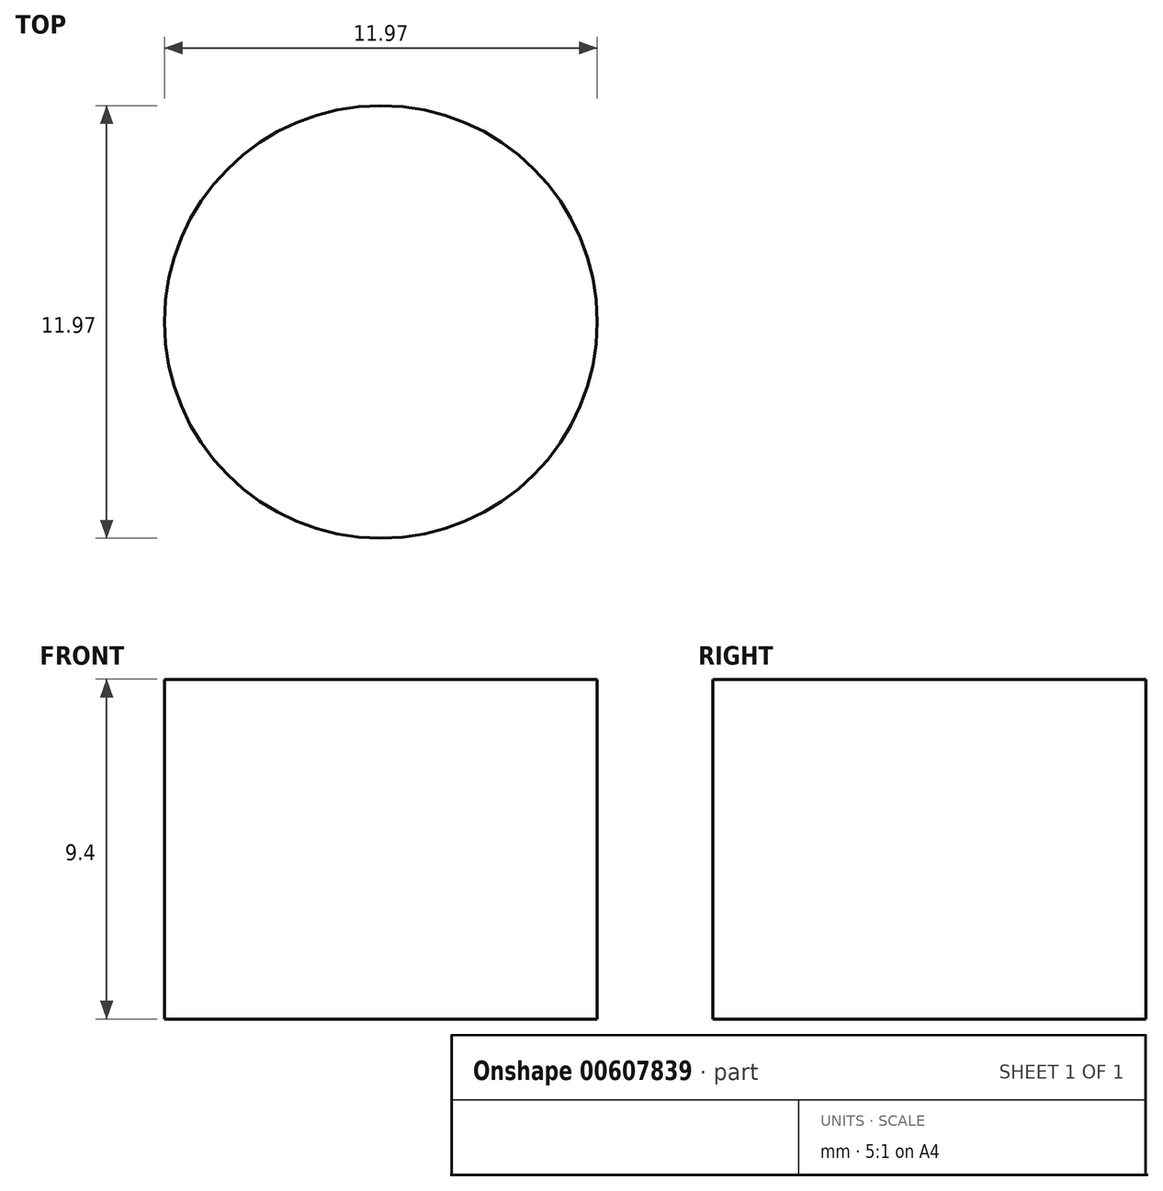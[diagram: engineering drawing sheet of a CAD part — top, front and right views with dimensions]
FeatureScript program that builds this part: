
annotation { "Feature Type Name" : "Feature", "Feature Type Description" : "" }
export const myFeature = defineFeature(function(context is Context, id is Id, definition is map)
    precondition{}
    {
        {
            var Q0;
            Q0=qCreatedBy(makeId("Top.planeOp"),FACE);
            var sketch = newSketch(context, id + "F0", { "sketchPlane" : qUnion([Q0])});
            skFitSpline(sketch, "E0", {"points": [v(-46, -42.9) * mm, v(-17.1, 34.94) * mm, v(23.83, -43.44) * mm], "startDerivative": vector(53.36, 235.08) * mm, "endDerivative": vector(86.14, -233.69) * mm});
            skSolve(sketch);
        }
        {
            var Q0;
            Q0=qCreatedBy(makeId("Top.planeOp"),FACE);
            var sketch = newSketch(context, id + "F1", { "sketchPlane" : qUnion([Q0])});
            skFitSpline(sketch, "E1", {"points": [v(-46, -43.23) * mm, v(-18.38, -23.65) * mm, v(24.18, -44.07) * mm], "startDerivative": vector(56.03, 61.14) * mm, "endDerivative": vector(83.58, -59.5) * mm});
            skSolve(sketch);
        }
        {
            var Q0;
            Q0=qCreatedBy(makeId("Top.planeOp"),FACE);
            var sketch = newSketch(context, id + "F2", { "sketchPlane" : qUnion([Q0])});
            skCircle(sketch, "E2", {"center": v(-16, 16.07) * mm, "radius": 5.99 * mm});
            skSolve(sketch);
        }
        {
            var Q0;
            Q0=qCreatedBy(makeId("Top.planeOp"),FACE);
            var sketch = newSketch(context, id + "F3", { "sketchPlane" : qUnion([Q0])});
            skSolve(sketch);
        }
        {
            var Q0;
            Q0 = qSketchRegion(id + "F3", true);
            var Q1;
            Q1 = qSketchRegion(id + "F0", true);
            var Q2;
            Q2 = qSketchRegion(id + "F1", true);
            var Q3;
            Q3 = qSketchRegion(id + "F0", true);
            var Q4;
            Q4 = qSketchRegion(id + "F2", true);
            var Q5;
            Q5 = qSketchRegion(id + "F1", true);
            var Q6;
            Q6 = qSketchRegion(id + "F0", true);
            var Q7;
            Q7 = qSketchRegion(id + "F3", true);
            extrude(context, id + "F4", {"entities" : qUnion([Q0, Q1, Q2, Q3, Q4, Q5, Q6, Q7]), "depth" : 9.4 * mm, "offsetDistance" : 25.4 * mm});
        }
        {
            var Q0;
            Q0=sQuery(id+"F1.wireOp",EDGE,"E1");
            var Q1;
            Q1=sQuery(id+"F0.wireOp",EDGE,"E0");
            extrude(context, id + "F5", {"bodyType" : ToolBodyType.SURFACE, "surfaceEntities" : qUnion([Q0, Q1]), "depth" : 9.4 * mm, "offsetDistance" : 25.4 * mm});
        }
    });
